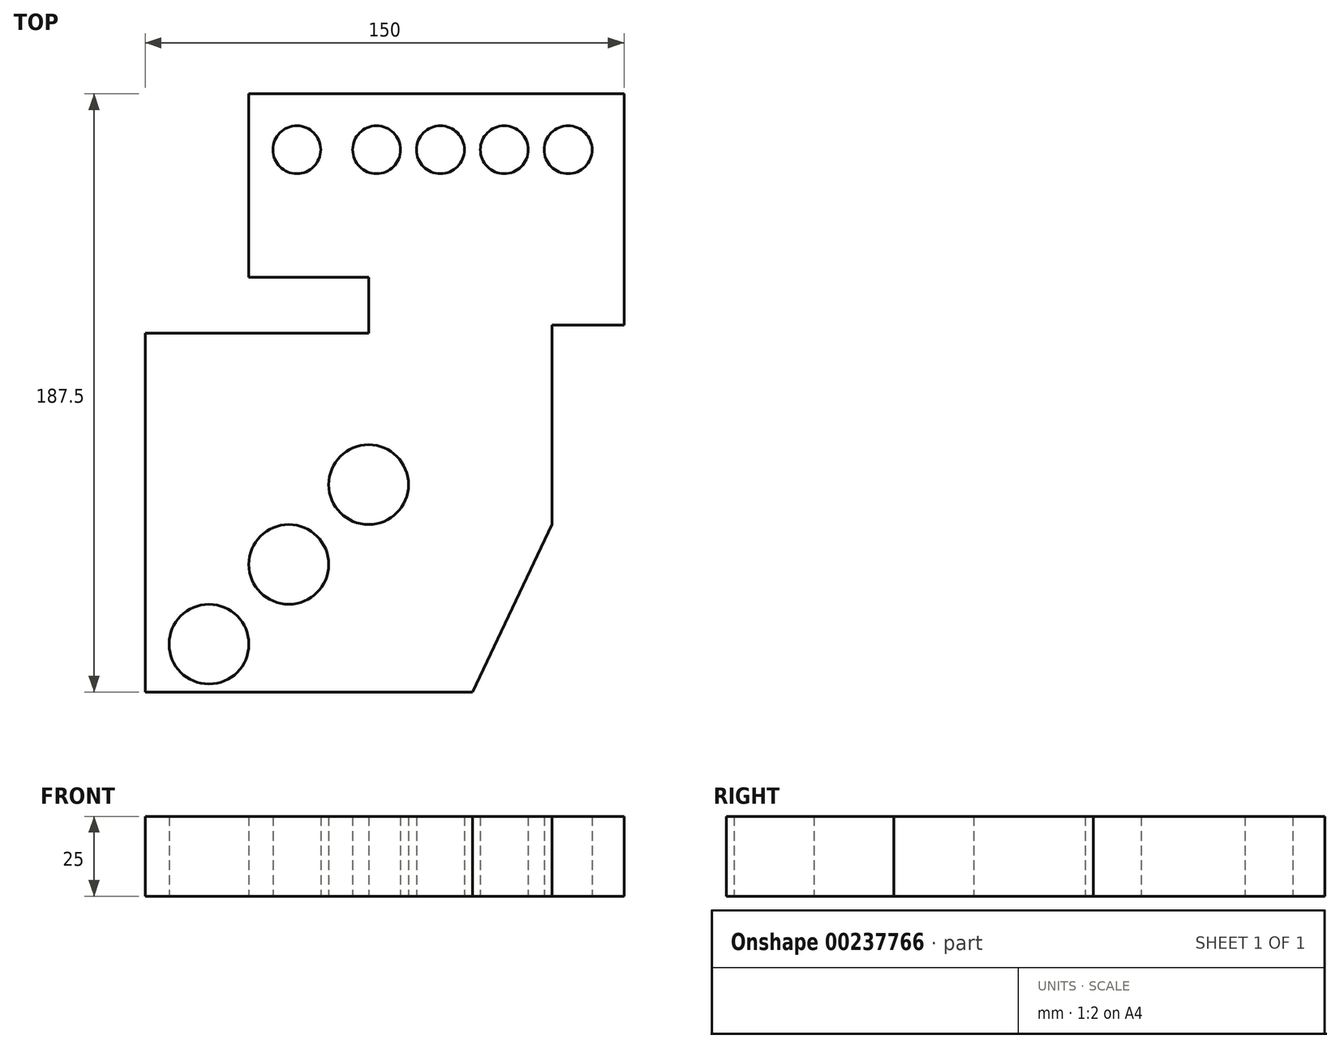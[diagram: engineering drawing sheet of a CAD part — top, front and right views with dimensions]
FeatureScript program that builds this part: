
annotation { "Feature Type Name" : "Feature", "Feature Type Description" : "" }
export const myFeature = defineFeature(function(context is Context, id is Id, definition is map)
    precondition{}
    {
        {
            var Q0;
            Q0=qCreatedBy(makeId("Top.planeOp"),FACE);
            var sketch = newSketch(context, id + "F0", { "sketchPlane" : qUnion([Q0])});
            skLineSegment(sketch, "E0", {"start": v(-83.57, -105.6) * mm, "end": v(18.93, -105.6) * mm});
            skLineSegment(sketch, "E1", {"start": v(18.93, -105.6) * mm, "end": v(43.93, -53.1) * mm});
            skLineSegment(sketch, "E2", {"start": v(-83.57, -105.6) * mm, "end": v(-83.57, 6.9) * mm});
            skLineSegment(sketch, "E3", {"start": v(-83.57, 6.9) * mm, "end": v(-13.57, 6.9) * mm});
            skLineSegment(sketch, "E4", {"start": v(-13.57, 6.9) * mm, "end": v(-13.57, 24.4) * mm});
            skLineSegment(sketch, "E5", {"start": v(-13.57, 24.4) * mm, "end": v(-51.07, 24.4) * mm});
            skLineSegment(sketch, "E6", {"start": v(-51.07, 24.4) * mm, "end": v(-51.07, 81.9) * mm});
            skLineSegment(sketch, "E7", {"start": v(66.43, 81.9) * mm, "end": v(66.43, 9.4) * mm});
            skLineSegment(sketch, "E8", {"start": v(66.43, 9.4) * mm, "end": v(43.93, 9.4) * mm});
            skLineSegment(sketch, "E9", {"start": v(43.93, 9.4) * mm, "end": v(43.93, -53.1) * mm});
            skLineSegment(sketch, "E10", {"start": v(-51.07, 81.9) * mm, "end": v(66.43, 81.9) * mm});
            skLineSegment(sketch, "E11", {"start": v(-83.57, -105.6) * mm, "end": v(-63.57, -105.6) * mm, "construction": true});
            skLineSegment(sketch, "E12", {"start": v(-63.57, -105.6) * mm, "end": v(-63.57, -90.6) * mm, "construction": true});
            skLineSegment(sketch, "E13", {"start": v(-63.57, -90.6) * mm, "end": v(-83.57, -90.6) * mm, "construction": true});
            skLineSegment(sketch, "E14", {"start": v(-63.57, -105.6) * mm, "end": v(-38.57, -105.6) * mm});
            skLineSegment(sketch, "E15", {"start": v(-38.57, -105.6) * mm, "end": v(-38.57, -65.6) * mm, "construction": true});
            skLineSegment(sketch, "E16", {"start": v(-38.57, -65.6) * mm, "end": v(-83.57, -65.6) * mm, "construction": true});
            skLineSegment(sketch, "E17", {"start": v(-38.57, -105.6) * mm, "end": v(-13.57, -105.6) * mm});
            skLineSegment(sketch, "E18", {"start": v(-13.57, -105.6) * mm, "end": v(-13.57, -40.6) * mm, "construction": true});
            skLineSegment(sketch, "E19", {"start": v(-13.57, -40.6) * mm, "end": v(-83.57, -40.6) * mm, "construction": true});
            skCircle(sketch, "E20", {"center": v(-63.57, -90.6) * mm, "radius": 12.5 * mm});
            skCircle(sketch, "E21", {"center": v(-38.57, -65.6) * mm, "radius": 12.5 * mm});
            skCircle(sketch, "E22", {"center": v(-13.57, -40.6) * mm, "radius": 12.5 * mm});
            skLineSegment(sketch, "E23", {"start": v(66.43, 81.9) * mm, "end": v(66.43, 99.76) * mm, "construction": true});
            skLineSegment(sketch, "E24", {"start": v(66.43, 99.76) * mm, "end": v(48.93, 99.76) * mm, "construction": true});
            skLineSegment(sketch, "E25", {"start": v(48.93, 99.76) * mm, "end": v(28.93, 99.76) * mm, "construction": true});
            skLineSegment(sketch, "E26", {"start": v(28.93, 99.76) * mm, "end": v(8.93, 99.76) * mm, "construction": true});
            skLineSegment(sketch, "E27", {"start": v(8.93, 99.76) * mm, "end": v(-11.07, 99.76) * mm, "construction": true});
            skLineSegment(sketch, "E28", {"start": v(-11.07, 99.76) * mm, "end": v(-36.07, 99.76) * mm, "construction": true});
            skLineSegment(sketch, "E29", {"start": v(48.93, 99.76) * mm, "end": v(48.93, 81.9) * mm, "construction": true});
            skLineSegment(sketch, "E30", {"start": v(48.93, 81.9) * mm, "end": v(48.93, 64.4) * mm, "construction": true});
            skLineSegment(sketch, "E31", {"start": v(28.93, 99.76) * mm, "end": v(28.93, 81.9) * mm, "construction": true});
            skLineSegment(sketch, "E32", {"start": v(28.93, 81.9) * mm, "end": v(28.93, 64.4) * mm, "construction": true});
            skLineSegment(sketch, "E33", {"start": v(8.93, 99.76) * mm, "end": v(8.93, 81.9) * mm, "construction": true});
            skLineSegment(sketch, "E34", {"start": v(8.93, 81.9) * mm, "end": v(8.93, 64.4) * mm, "construction": true});
            skLineSegment(sketch, "E35", {"start": v(-11.07, 99.76) * mm, "end": v(-11.07, 81.9) * mm, "construction": true});
            skLineSegment(sketch, "E36", {"start": v(-11.07, 81.9) * mm, "end": v(-11.07, 64.4) * mm, "construction": true});
            skLineSegment(sketch, "E37", {"start": v(-36.07, 99.76) * mm, "end": v(-36.07, 81.9) * mm, "construction": true});
            skLineSegment(sketch, "E38", {"start": v(-36.07, 81.9) * mm, "end": v(-36.07, 64.4) * mm, "construction": true});
            skCircle(sketch, "E39", {"center": v(-36.07, 64.4) * mm, "radius": 7.5 * mm});
            skCircle(sketch, "E40", {"center": v(-11.07, 64.4) * mm, "radius": 7.5 * mm});
            skCircle(sketch, "E41", {"center": v(8.93, 64.4) * mm, "radius": 7.5 * mm});
            skCircle(sketch, "E42", {"center": v(28.93, 64.4) * mm, "radius": 7.5 * mm});
            skCircle(sketch, "E43", {"center": v(48.93, 64.4) * mm, "radius": 7.5 * mm});
            skSolve(sketch);
        }
        {
            var Q0;
            Q0 = qSketchRegion(id + "F0", true);
            extrude(context, id + "F1", {"entities" : qUnion([Q0]), "depth" : 25 * mm});
        }
    });
